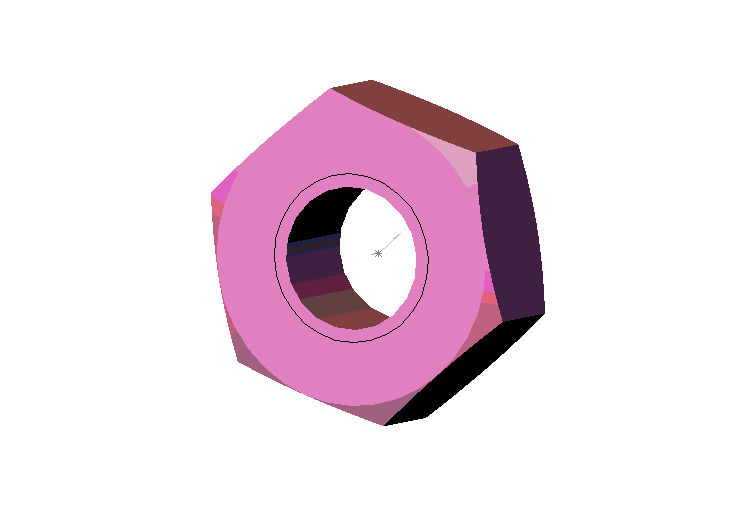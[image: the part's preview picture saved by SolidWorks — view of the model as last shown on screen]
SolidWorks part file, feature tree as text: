
SOLIDWORKS PART (.sldprt)
format: sldprt  version: not decoded by parser v0  size: 189,440 bytes
history: native  units: mm
features: sketch x4, plane x3, material x1, revolve x1, cut_extrude x1, hole x1, thread x1 (+9 scaffold rows collapsed)
feature tree (21):
  scaffold x9  (default folders/planes/origin — collapsed)
  material  "Matériau <non spécifié>"
  plane  "Plan1"
  plane  "Plan2"
  plane  "Plan3"
  sketch  "Esquisse1"  dims[c1.D1=17.0mm c1.D2=25.0mm c1.D3=5.0mm c1.D4=~36.459934mm c2.D4=20.0deg c2.D2=25.0mm c2.D1=5.0mm c3.D2=17.0mm c3.D3=~9.896945mm c4.D3=40.0deg c4.D4=25.0mm c5.D4=20.0deg c5.D5=25.0mm c5.D1=12.5mm c5.D2=7.5mm c5.D3=5.0mm c6.D1=~15.333879mm c7.D1=60.0deg c7.D2=~23.63068mm c8.D2=20.0deg c9.D2=12.5mm c9.D3=7.0mm c9.D4=6.0mm]
  revolve  "Base-Révolution"  Angle=360deg
  sketch  "Esquisse2"  dims[c1.D3=25.0mm c1.D1=17.0mm c1.D2=~9.790762mm c2.D2=~118.979711deg c2.D3=~9.790762mm c3.D3=~120.510144deg c3.D2=~9.790762mm c4.D2=~118.979711deg c5.D2=~9.790762mm c6.D2=~120.510144deg c7.D2=~9.790762mm c8.D2=~118.979711deg c8.D1=~5.151302mm c9.D1=120.0deg c9.D2=17.0mm c9.D3=10.0mm]
  cut_extrude  "Enlèv. mat.-Extru.1"  [1 undecoded]
  hole  "Perçage2"  Diameter=6.8mm Depth=22.25mm
  sketch  "Esquisse6"
  sketch  "Esquisse5"  dims[hole-wizard template sketch: 46 standard entries collapsed; hole parameters kept: c15.Diamètre du perçage=6.8mm c15.Profondeur du perçage=22.25mm c15.D3=~14.816244mm c15.Angle de pointe=118.0deg]
  thread  "Représentation de filetage3"  Diameter=6mm  [1 undecoded]
decode coverage: 6 of 8 modeling features carry decoded parameters
note: ~ marks probable driven/reference dimensions
note: 2 parameter values undecoded
note: suppression state not decoded; provenance and decode notes live in map.json
